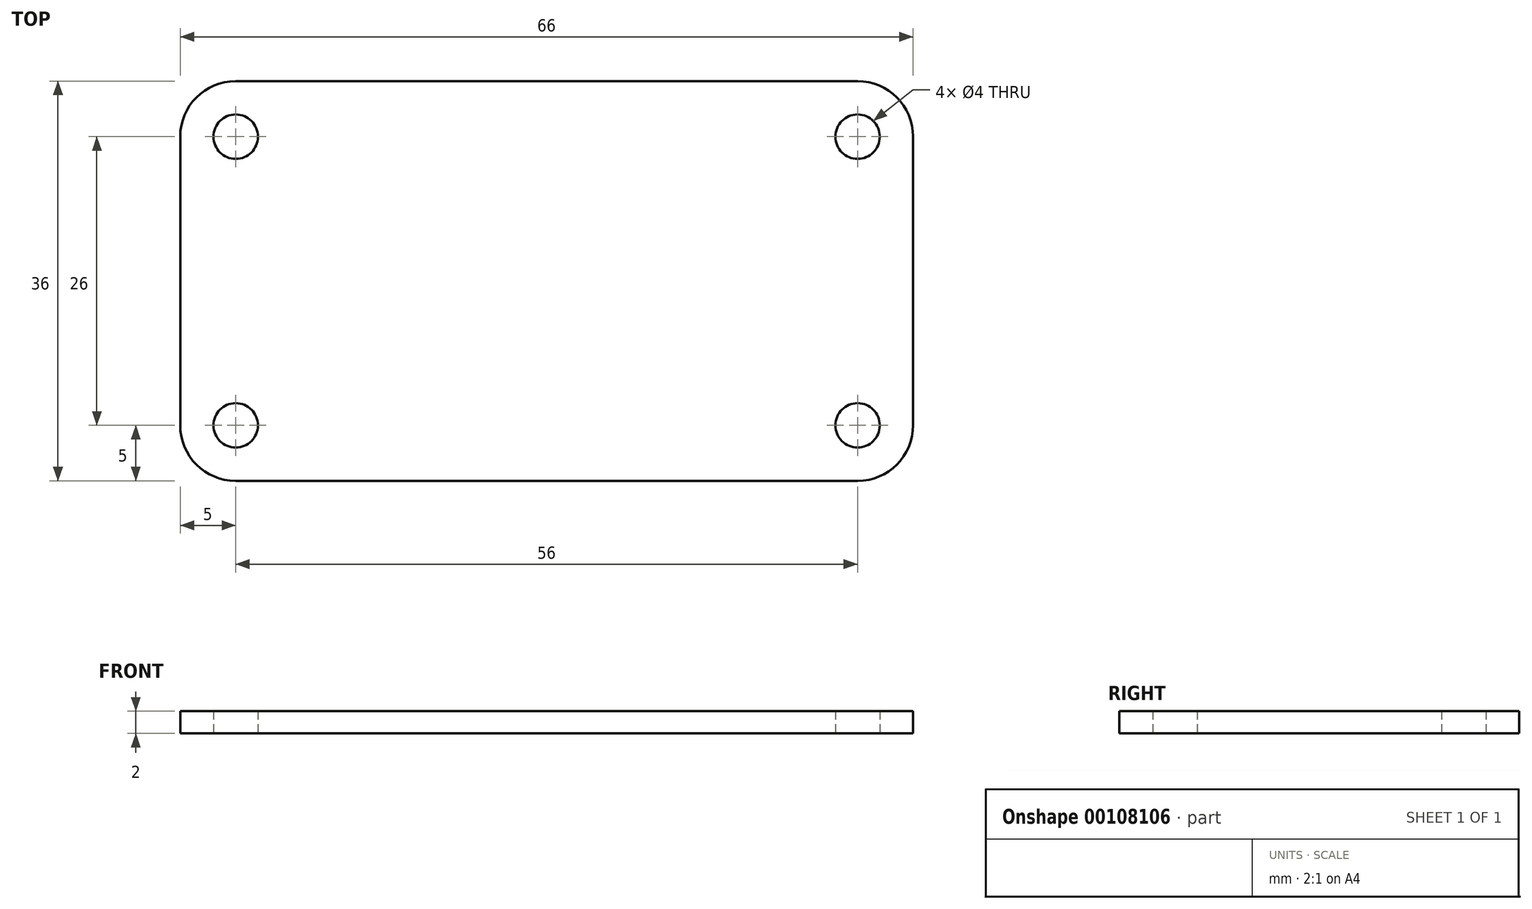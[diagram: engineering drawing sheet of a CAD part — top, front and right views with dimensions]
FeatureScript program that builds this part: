
annotation { "Feature Type Name" : "Feature", "Feature Type Description" : "" }
export const myFeature = defineFeature(function(context is Context, id is Id, definition is map)
    precondition{}
    {
        {
            var Q0;
            Q0=qCreatedBy(makeId("Top.planeOp"),FACE);
            var sketch = newSketch(context, id + "F0", { "sketchPlane" : qUnion([Q0])});
            skPoint(sketch, "E0.middle", {"position": v(0, 0) * mm});
            skLineSegment(sketch, "E1.0", {"start": v(28, 18) * mm, "end": v(-28, 18) * mm});
            skLineSegment(sketch, "E1.1", {"start": v(33, -13) * mm, "end": v(33, 13) * mm});
            skLineSegment(sketch, "E1.2", {"start": v(28, -18) * mm, "end": v(-28, -18) * mm});
            skLineSegment(sketch, "E1.3", {"start": v(-33, -13) * mm, "end": v(-33, 13) * mm});
            skPoint(sketch, "E2.visualSharp", {"position": v(-33, 18) * mm});
            skArc(sketch, "E2.filletArc", {"start": v(-28, 18) * mm, "mid": v(-31.54, 16.54) * mm, "end": v(-33, 13) * mm});
            skPoint(sketch, "E3.visualSharp", {"position": v(33, 18) * mm});
            skArc(sketch, "E3.filletArc", {"start": v(33, 13) * mm, "mid": v(31.54, 16.54) * mm, "end": v(28, 18) * mm});
            skPoint(sketch, "E4.visualSharp", {"position": v(33, -18) * mm});
            skArc(sketch, "E4.filletArc", {"start": v(28, -18) * mm, "mid": v(31.54, -16.54) * mm, "end": v(33, -13) * mm});
            skPoint(sketch, "E5.visualSharp", {"position": v(-33, -18) * mm});
            skArc(sketch, "E5.filletArc", {"start": v(-33, -13) * mm, "mid": v(-31.54, -16.54) * mm, "end": v(-28, -18) * mm});
            skCircle(sketch, "E6", {"center": v(-28, 13) * mm, "radius": 2 * mm});
            skCircle(sketch, "E7", {"center": v(28, -13) * mm, "radius": 2 * mm});
            skCircle(sketch, "E8", {"center": v(28, 13) * mm, "radius": 2 * mm});
            skCircle(sketch, "E9", {"center": v(-28, -13) * mm, "radius": 2 * mm});
            skSolve(sketch);
        }
        {
            var Q0;
            Q0 = qSketchRegion(id + "F0", true);
            extrude(context, id + "F1", {"entities" : qUnion([Q0]), "depth" : 2 * mm, "offsetDistance" : 25 * mm});
        }
    });
